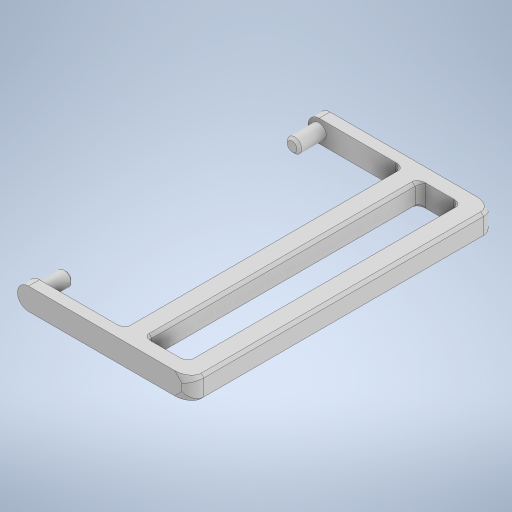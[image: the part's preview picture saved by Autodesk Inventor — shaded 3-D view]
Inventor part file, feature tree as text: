
AUTODESK INVENTOR PART (.ipt)
format: ipt  version: 2023 (Build 270158000, 158)  size: 333,824 bytes
history: native  units: in
note: dims shown in document units (in); Inventor stores cm internally (conversion verified against a paired STEP export)
features: extrude x4, sketch x4, fillet x2, thicken_offset x2, mirror x1, chamfer x1
ambient origin geometry x8: Origin, YZ Plane, XZ Plane, XY Plane, X Axis, Y Axis, Z Axis, Center Point
bodies: Solid1 (feature_tree)
feature tree (14):
  extrude  "Extrusion1"  Depth=0.1575in
  extrude  "Extrusion2"  Depth=2.0079in TaperAngle=0.0deg
  extrude  "Extrusion3"  Depth=0.0787in
  mirror  "Mirror1"
  extrude  "Extrusion4"  Depth=0.1575in
  chamfer  "Chamfer1"  Distance=1.9685in
  fillet  "Fillet1"  Radius=0.0197in
  fillet  "Fillet3"  Radius=0.0787in
  thicken_offset  "Thicken1"
  thicken_offset  "Thicken2"
  sketch  "Sketch1"  dims[d0=0.1575in d1=1.2598in]
  sketch  "Sketch2"  dims[d2=2.1654in d3=0.0in d4=2.0079in d5=0.0in]
  sketch  "Sketch3"  dims[d6=0.1102in d7=0.0787in]
  sketch  "Sketch4"  dims[d8=0.1969in d9=0.0in d10=0.1575in d12=1.9685in d13=0.0in d14=0.0197in d15=0.0787in d16=45.0deg d20=0.0787in d22=0.0394in d23=0.1969in d24=0.0394in d25=0.0039in d26=0.0039in d27=0.0039in d28=0.0039in]
